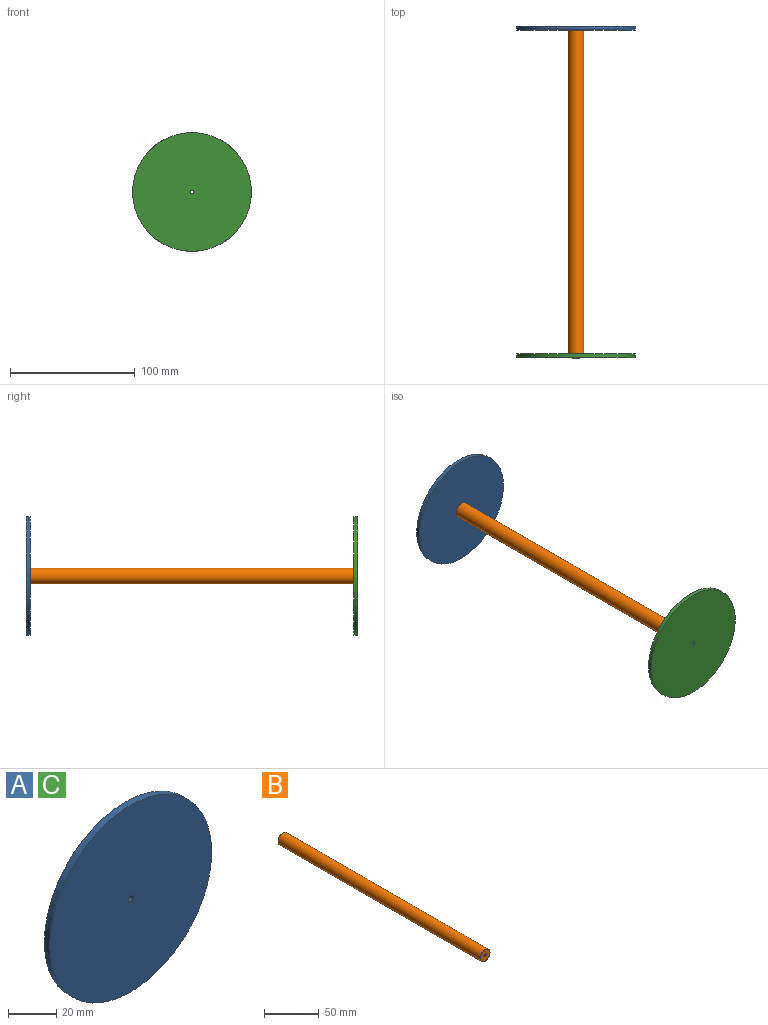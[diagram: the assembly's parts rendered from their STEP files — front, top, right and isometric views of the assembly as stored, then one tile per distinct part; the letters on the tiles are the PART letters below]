
ASSEMBLY  parts=3 mates=2
PART A: 4 faces, bbox 95.3x3.2x95.3 mm
  f0: cylinder r=1.59mm len=3.18mm, axis (0,1,0), area 31.7mm2, adj f2,f3
  f1: cylinder r=47.62mm len=95.25mm, axis (0,1,0), area 950.1mm2, adj f2,f3
  f2: plane 95.25x95.25mm, normal (0,-1,0), area 7117.7mm2, adj f0,f1
  f3: plane 95.25x95.25mm, normal (0,1,0), area 7117.7mm2, adj f0,f1
PART B: 4 faces, bbox 12.7x260x12.7 mm
  f0: cylinder r=1.59mm len=260mm, axis (0,1,0), area 2593.4mm2, adj f2,f3
  f1: cylinder r=6.35mm len=260mm, axis (0,1,0), area 10373.5mm2, adj f2,f3
  f2: plane 12.7x12.7mm, normal (0,-1,0), area 118.8mm2, adj f0,f1
  f3: plane 12.7x12.7mm, normal (0,1,0), area 118.8mm2, adj f0,f1
PART C: same geometry as A
PLACE A t=(-57.86,107.7,11.89)mm
PLACE B t=(-57.86,-25.48,11.89)mm
PLACE C rot(axis=(1,0,0),180deg) t=(-57.86,-158.65,11.89)mm
MATE revolute A.f0 <-> B.f0  axis (0,-1,0) through (-57.86,104.52,11.89)mm
MATE revolute C.f0 <-> B.f0  axis (0,1,0) through (-57.86,-155.48,11.89)mm
